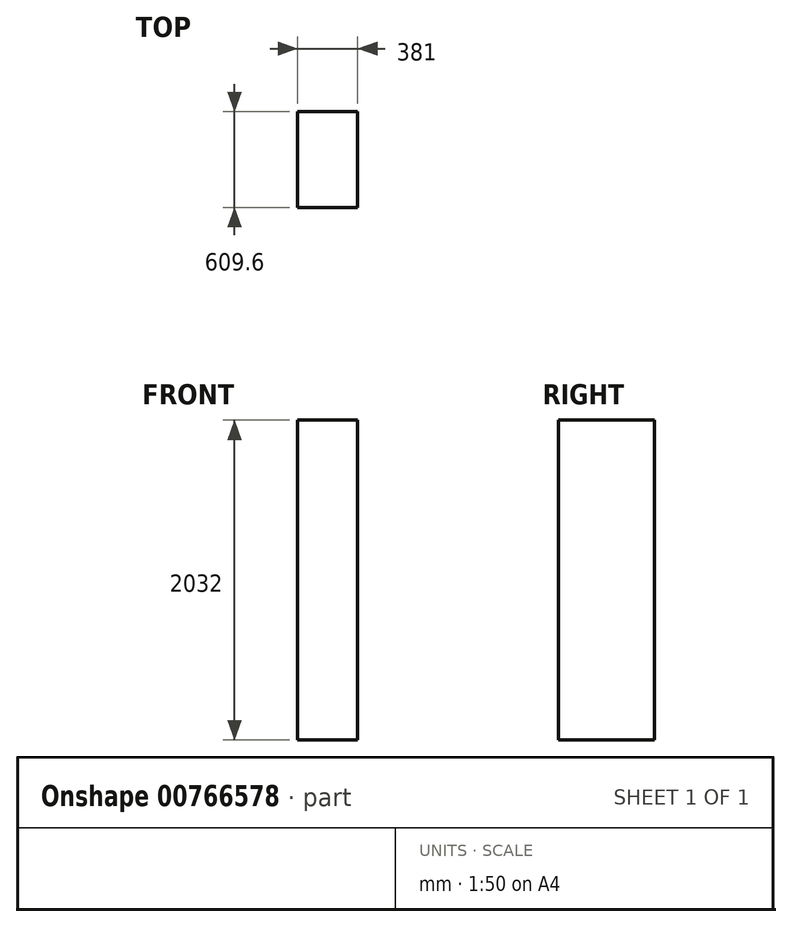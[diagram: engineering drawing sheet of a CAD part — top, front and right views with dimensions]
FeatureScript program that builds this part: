
annotation { "Feature Type Name" : "Feature", "Feature Type Description" : "" }
export const myFeature = defineFeature(function(context is Context, id is Id, definition is map)
    precondition{}
    {
        {
            var Q0;
            Q0=qCreatedBy(makeId("Top.planeOp"),FACE);
            var sketch = newSketch(context, id + "F0", { "sketchPlane" : qUnion([Q0])});
            skLineSegment(sketch, "E0.bottom", {"start": v(-190.5, 304.8) * mm, "end": v(190.5, 304.8) * mm});
            skLineSegment(sketch, "E0.top", {"start": v(-190.5, -304.8) * mm, "end": v(190.5, -304.8) * mm});
            skLineSegment(sketch, "E0.left", {"start": v(-190.5, 304.8) * mm, "end": v(-190.5, -304.8) * mm});
            skLineSegment(sketch, "E0.right", {"start": v(190.5, 304.8) * mm, "end": v(190.5, -304.8) * mm});
            skLineSegment(sketch, "E1", {"start": v(-190.5, 304.8) * mm, "end": v(190.5, -304.8) * mm, "construction": true});
            skSolve(sketch);
        }
        {
            var Q0;
            Q0=qSketchRegion(id+"F0",true);
            extrude(context, id + "F1", {"entities" : qUnion([Q0]), "depth" : 2032 * mm, "offsetDistance" : 25.4 * mm});
        }
    });
